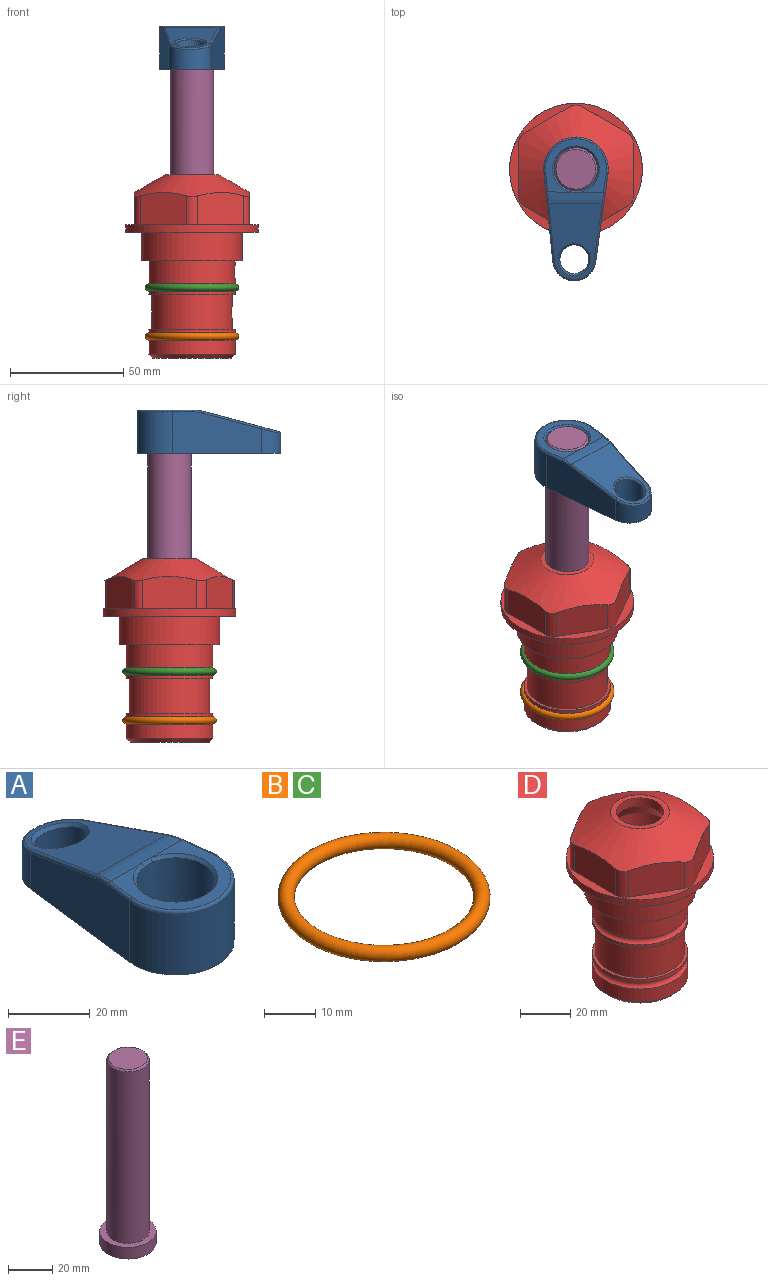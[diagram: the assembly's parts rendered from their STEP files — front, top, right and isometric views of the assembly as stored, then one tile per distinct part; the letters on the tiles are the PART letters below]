
ASSEMBLY  parts=5 mates=4
PART A: 31 faces, bbox 31.7x65.5x19.8 mm
  f0: plane 39.12x18.26mm, normal (0.99,0.12,0), area 612.2mm2, adj f1,f4,f7,f11,f13,f15
  f1: cylinder r=9.53mm len=18.91mm, axis (0,0,-1), area 296.1mm2, adj f0,f2,f7,f17
  f2: plane 39.12x18.26mm, normal (-0.99,0.12,0), area 612.2mm2, adj f1,f4,f7,f12,f14,f16
  f3: cylinder r=6.35mm len=12.7mm, axis (0,0,-1), area 362.4mm2, adj f7,f18
  f4: cylinder r=14.29mm len=28.58mm, axis (0,0,-1), area 882.2mm2, adj f0,f2,f7,f10
  f5: cylinder r=9.53mm len=19.05mm, axis (0,0,-1), area 1092.6mm2, adj f7,f19,f20
  f6: plane 26.99x23.69mm, normal (0,0,1), area 216.2mm2, adj f9,f10,f11,f12,f19
  f7: plane 63.5x28.58mm, normal (0,0,-1), area 661.8mm2, adj f0,f1,f2,f3,f4,f5,f22,f23
  f8: plane 33.52x23.6mm, normal (0,0.26,0.97), area 486mm2, adj f9,f15,f16,f17,f18
  f9: cylinder r=19.05mm len=24.72mm, axis (1,0,0), area 120.4mm2, adj f6,f8,f13,f14,f20
  f10: torus R=13.49mm, axis (0,0,1), area 59mm2, adj f4,f6,f11,f12
  f11: cylinder r=0.79mm len=8.67mm, axis (0.12,-0.99,0), area 10.8mm2, adj f0,f6,f10,f13
  f12: cylinder r=0.79mm len=8.67mm, axis (0.12,0.99,0), area 10.8mm2, adj f2,f6,f10,f14
  f13: bspline ~4.95x1.42mm, area 6.1mm2, adj f0,f9,f11,f15
  f14: bspline ~4.95x1.42mm, area 6.1mm2, adj f2,f9,f12,f16
  f15: cylinder r=0.79mm len=25.95mm, axis (0.12,-0.96,0.26), area 32.9mm2, adj f0,f8,f13,f17
  f16: cylinder r=0.79mm len=25.95mm, axis (0.12,0.96,-0.26), area 32.9mm2, adj f2,f8,f14,f17
  f17: bspline ~18.91x8.38mm, area 30mm2, adj f1,f8,f15,f16
  f18: bspline ~14.29x14.29mm, area 48.3mm2, adj f3,f8
  f19: cone r=9.53mm half-angle=45deg, axis (0,0,1), area 66.5mm2, adj f5,f6,f20
  f20: bspline ~3.22x0.96mm, area 3.5mm2, adj f5,f9,f19
  f21: plane 2.75x2.72mm, normal (0,0,-1), area 2.9mm2, adj f23,f25,f28
  f22: plane 23.05x15.88mm, normal (-0.99,-0.12,0), area 323.6mm2, adj f7,f25,f26,f27,f28,f29
  f23: plane 23.05x15.88mm, normal (0.99,-0.12,0), area 323.6mm2, adj f7,f21,f25,f27,f28,f30
  f24: cylinder r=9.53mm len=10.69mm, axis (0,0,-1), area 114.7mm2, adj f7,f27,f29,f30
  f25: cylinder r=12.7mm len=20.59mm, axis (0,0,-1), area 381.1mm2, adj f7,f21,f22,f23,f26,f28
  f26: plane 2.75x2.72mm, normal (0,0,-1), area 2.9mm2, adj f22,f25,f28
  f27: plane 19.72x18.37mm, normal (0,-0.26,-0.97), area 291.8mm2, adj f22,f23,f24,f28,f29,f30
  f28: cylinder r=15.88mm len=19.92mm, axis (1,0,0), area 54.8mm2, adj f21,f22,f23,f25,f26,f27
  f29: cylinder r=1.59mm len=11mm, axis (0,0,-1), area 34.7mm2, adj f7,f22,f24,f27
  f30: cylinder r=1.59mm len=11mm, axis (0,0,-1), area 34.7mm2, adj f7,f23,f24,f27
PART B: 1 faces, bbox 44.7x44.7x3.2 mm
  f0: torus R=19.05mm, axis (0,0,1), area 1193.9mm2
PART C: same geometry as B
PART D: 36 faces, bbox 58.7x58.7x81 mm
  f0: cylinder r=17.78mm len=35.56mm, axis (0,0,1), area 1670.8mm2, adj f23,f24,f31
  f1: cylinder r=19.05mm len=38.1mm, axis (0,0,1), area 1191.9mm2, adj f26,f27,f30
  f2: plane 58.66x58.66mm, normal (0,0,-1), area 1150.6mm2, adj f3,f28
  f3: cylinder r=29.33mm len=58.66mm, axis (0,0,-1), area 585.1mm2, adj f2,f4
  f4: plane 58.66x58.66mm, normal (0,0,1), area 475.9mm2, adj f3,f5,f6,f7,f8,f9,f10,f11
  f5: plane 20.32x14.34mm, normal (-0.5,0.87,0), area 324.4mm2, adj f4,f15,f16,f17
  f6: plane 20.32x14.34mm, normal (0.5,0.87,0), area 324.4mm2, adj f4,f14,f15,f17
  f7: plane 23.48x14.34mm, normal (1,0,0), area 324.4mm2, adj f4,f13,f14,f17
  f8: plane 20.32x14.34mm, normal (0.5,-0.87,0), area 324.4mm2, adj f4,f12,f13,f17
  f9: plane 20.32x14.34mm, normal (-0.5,-0.87,0), area 324.4mm2, adj f4,f11,f12,f17
  f10: plane 23.48x14.34mm, normal (-1,0,0), area 324.4mm2, adj f4,f11,f16,f17
  f11: cylinder r=5.08mm len=12.85mm, axis (0,0,-1), area 67.2mm2, adj f4,f9,f10,f17
  f12: cylinder r=5.08mm len=12.85mm, axis (0,0,-1), area 67.2mm2, adj f4,f8,f9,f17
  f13: cylinder r=5.08mm len=12.85mm, axis (0,0,-1), area 67.2mm2, adj f4,f7,f8,f17
  f14: cylinder r=5.08mm len=12.85mm, axis (0,0,-1), area 67.2mm2, adj f4,f6,f7,f17
  f15: cylinder r=5.08mm len=12.85mm, axis (0,0,-1), area 67.2mm2, adj f4,f5,f6,f17
  f16: cylinder r=5.08mm len=12.85mm, axis (0,0,-1), area 67.2mm2, adj f4,f5,f10,f17
  f17: cone r=11.73mm half-angle=60deg, axis (0,0,-1), area 2071.8mm2, adj f5,f6,f7,f8,f9,f10,f11,f12
  f18: plane 23.46x23.46mm, normal (0,0,1), area 147.4mm2, adj f17,f35
  f19: plane 34.93x34.93mm, normal (0,0,-1), area 958mm2, adj f29
  f20: cylinder r=19.05mm len=38.1mm, axis (0,0,1), area 760.1mm2, adj f21,f29
  f21: torus R=19.05mm, axis (0,0,1), area 565.3mm2, adj f20,f22
  f22: cylinder r=19.05mm len=38.1mm, axis (0,0,1), area 190mm2, adj f21,f23
  f23: plane 38.1x38.1mm, normal (0,0,1), area 146.9mm2, adj f0,f22
  f24: plane 38.1x38.1mm, normal (0,0,-1), area 146.9mm2, adj f0,f25
  f25: cylinder r=19.05mm len=38.1mm, axis (0,0,1), area 190mm2, adj f24,f26
  f26: torus R=19.05mm, axis (0,0,1), area 565.3mm2, adj f1,f25
  f27: plane 44.45x44.45mm, normal (0,0,-1), area 411.7mm2, adj f1,f28
  f28: cylinder r=22.23mm len=44.45mm, axis (0,0,1), area 1773.5mm2, adj f2,f27
  f29: cone r=19.05mm half-angle=45deg, axis (0,0,1), area 257.5mm2, adj f19,f20
  f30: cylinder r=3.17mm len=6.75mm, axis (-1,0,0), area 128mm2, adj f1,f33
  f31: cylinder r=3.17mm len=6.35mm, axis (-1,0,0), area 102.5mm2, adj f0,f33
  f32: plane 25.4x25.4mm, normal (0,0,1), area 506.7mm2, adj f33
  f33: cylinder r=12.7mm len=66.42mm, axis (0,0,-1), area 5236.2mm2, adj f30,f31,f32,f34
  f34: cone r=9.53mm half-angle=30deg, axis (0,0,-1), area 443.4mm2, adj f33,f35
  f35: cylinder r=9.53mm len=19.05mm, axis (0,0,-1), area 240.9mm2, adj f18,f34
PART E: 6 faces, bbox 25.4x25.4x101.6 mm
  f0: plane 17.46x17.46mm, normal (0,0,1), area 239.5mm2, adj f5
  f1: plane 25.4x25.4mm, normal (0,0,-1), area 506.7mm2, adj f2
  f2: cylinder r=12.7mm len=25.4mm, axis (0,0,1), area 506.7mm2, adj f1,f3
  f3: plane 25.4x25.4mm, normal (0,0,1), area 221.7mm2, adj f2,f4
  f4: cylinder r=9.53mm len=94.46mm, axis (0,0,1), area 5653mm2, adj f3,f5
  f5: cone r=8.73mm half-angle=45deg, axis (0,0,-1), area 64.4mm2, adj f0,f4
PLACE A rot(axis=(0,0,1),178.9deg) t=(0,0,27.55)mm
PLACE B t=(0,0,-21.59)mm
PLACE C at identity
PLACE D at identity fixed
PLACE E rot(axis=(0,0,1),178.9deg) t=(0,0,27.55)mm
MATE fastened D.f0 <-> B.f0  axis (0,0,1) through (0,0,-46.1)mm
MATE cylindrical D.f0 <-> E.f2  axis (0,0,1) through (0,0,-50.55)mm
MATE fastened D.f0 <-> C.f0  axis (0,0,1) through (0,0,-24.51)mm
MATE fastened E.f2 <-> A.f4  axis (0,0,1) through (0,0,91.05)mm
